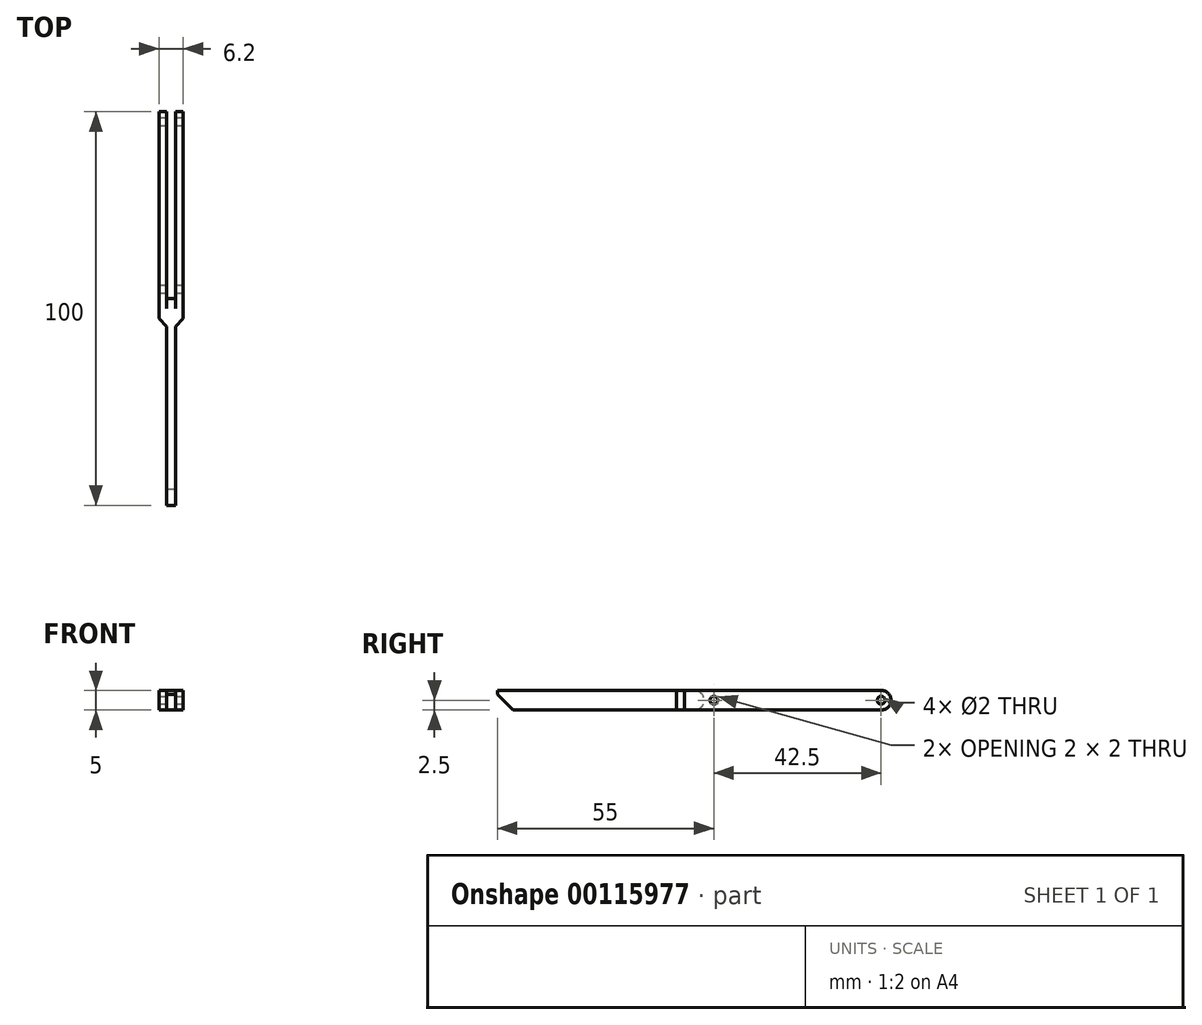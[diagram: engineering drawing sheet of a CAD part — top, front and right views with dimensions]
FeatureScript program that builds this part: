
annotation { "Feature Type Name" : "Feature", "Feature Type Description" : "" }
export const myFeature = defineFeature(function(context is Context, id is Id, definition is map)
    precondition{}
    {
        {
            var Q0;
            Q0=qCreatedBy(makeId("Top.planeOp"),FACE);
            var sketch = newSketch(context, id + "F0", { "sketchPlane" : qUnion([Q0])});
            skLineSegment(sketch, "E0", {"start": v(0, -50) * mm, "end": v(1.1, -50) * mm});
            skLineSegment(sketch, "E1", {"start": v(1.1, -50) * mm, "end": v(1.1, -2.5) * mm});
            skLineSegment(sketch, "E2", {"start": v(1.1, -2.5) * mm, "end": v(3.1, -2.5) * mm});
            skLineSegment(sketch, "E3", {"start": v(3.1, -2.5) * mm, "end": v(3.1, 50) * mm});
            skLineSegment(sketch, "E4", {"start": v(3.1, 50) * mm, "end": v(1.1, 50) * mm});
            skLineSegment(sketch, "E5", {"start": v(1.1, 50) * mm, "end": v(1.1, 2.5) * mm});
            skLineSegment(sketch, "E6", {"start": v(1.1, 2.5) * mm, "end": v(0, 2.5) * mm});
            skLineSegment(sketch, "E7.MirrorCS", {"start": v(-1.1, 2.5) * mm, "end": v(0, 2.5) * mm});
            skLineSegment(sketch, "E8.MirrorCS", {"start": v(-3.1, -2.5) * mm, "end": v(-3.1, 50) * mm});
            skLineSegment(sketch, "E9.MirrorCS", {"start": v(-1.1, -2.5) * mm, "end": v(-3.1, -2.5) * mm});
            skLineSegment(sketch, "E10.MirrorCS", {"start": v(-3.1, 50) * mm, "end": v(-1.1, 50) * mm});
            skLineSegment(sketch, "E11.MirrorCS", {"start": v(0, -50) * mm, "end": v(-1.1, -50) * mm});
            skLineSegment(sketch, "E12.MirrorCS", {"start": v(-1.1, -50) * mm, "end": v(-1.1, -2.5) * mm});
            skLineSegment(sketch, "E13.MirrorCS", {"start": v(-1.1, 50) * mm, "end": v(-1.1, 2.5) * mm});
            skSolve(sketch);
        }
        {
            var Q0;
            Q0=makeQuery(id+"F0.imprint","IMPRINT",FACE,{"disambiguationData":[TD([[makeQuery(id+"F0.imprint","IMPRINT",EDGE,{"derivedFrom":sQuery(id+"F0.wireOp",EDGE,"E0")}),1.0]])]});
            extrude(context, id + "F1", {"entities" : qUnion([Q0]), "endBound" : BoundingType.SYMMETRIC, "depth" : 5 * mm});
        }
        {
            var Q0;
            Q0=makeQuery(id+"F1.opExtrude","CAP_EDGE",EDGE,{"disambiguationData":[OSD([sQuery(id+"F0.wireOp",EDGE,"E0"),sQuery(id+"F0.wireOp",EDGE,"E11.MirrorCS")])],"isStart":true});
            chamfer(context, id + "F2", {"entities" : qUnion([Q0]), "width" : 4 * mm, "tangentPropagation" : true});
        }
        {
            var Q0;
            Q0=makeQuery(id+"F1.opExtrude","SWEPT_EDGE",EDGE,{"disambiguationData":[OSD([sQuery(id+"F0.wireOp",EDGE,"E1"),sQuery(id+"F0.wireOp",EDGE,"E2")])]});
            var Q1;
            Q1=makeQuery(id+"F1.opExtrude","SWEPT_EDGE",EDGE,{"disambiguationData":[OSD([sQuery(id+"F0.wireOp",EDGE,"E9.MirrorCS"),sQuery(id+"F0.wireOp",EDGE,"E12.MirrorCS")])]});
            chamfer(context, id + "F3", {"entities" : qUnion([Q0, Q1]), "width" : 2 * mm, "tangentPropagation" : true});
        }
        {
            var Q0;
            Q0=makeQuery(id+"F1.opExtrude","CAP_EDGE",EDGE,{"disambiguationData":[OSD([sQuery(id+"F0.wireOp",EDGE,"E4")])],"isStart":false});
            var Q1;
            Q1=makeQuery(id+"F1.opExtrude","CAP_EDGE",EDGE,{"disambiguationData":[OSD([sQuery(id+"F0.wireOp",EDGE,"E10.MirrorCS")])],"isStart":false});
            var Q2;
            Q2=makeQuery(id+"F1.opExtrude","CAP_EDGE",EDGE,{"disambiguationData":[OSD([sQuery(id+"F0.wireOp",EDGE,"E10.MirrorCS")])],"isStart":true});
            var Q3;
            Q3=makeQuery(id+"F1.opExtrude","CAP_EDGE",EDGE,{"disambiguationData":[OSD([sQuery(id+"F0.wireOp",EDGE,"E4")])],"isStart":true});
            var Q4;
            Q4=makeQuery(id+"F1.opExtrude","CAP_EDGE",EDGE,{"disambiguationData":[OSD([sQuery(id+"F0.wireOp",EDGE,"E6"),sQuery(id+"F0.wireOp",EDGE,"E7.MirrorCS")])],"isStart":true});
            var Q5;
            Q5=makeQuery(id+"F1.opExtrude","CAP_EDGE",EDGE,{"disambiguationData":[OSD([sQuery(id+"F0.wireOp",EDGE,"E6"),sQuery(id+"F0.wireOp",EDGE,"E7.MirrorCS")])],"isStart":false});
            fillet(context, id + "F4", {"entities" : qUnion([Q0, Q1, Q2, Q3, Q4, Q5]), "radius" : 2.5 * mm, "tangentPropagation" : true, "allowEdgeOverflow" : false});
        }
        {
            var Q0;
            Q0=qCreatedBy(makeId("Right.planeOp"),FACE);
            var sketch = newSketch(context, id + "F5", { "sketchPlane" : qUnion([Q0])});
            skCircle(sketch, "E14", {"center": v(5, 0) * mm, "radius": 1 * mm});
            skCircle(sketch, "E15", {"center": v(47.5, 0) * mm, "radius": 1 * mm});
            skCircle(sketch, "E16", {"center": v(5, 0) * mm, "radius": 2.5 * mm, "construction": true});
            skSolve(sketch);
        }
        {
            var Q0;
            Q0 = qSketchRegion(id + "F5", true);
            extrude(context, id + "F6", {"entities" : qUnion([Q0]), "operationType" : NewBodyOperationType.REMOVE, "endBound" : BoundingType.THROUGH_ALL, "oppositeDirection" : true, "depth" : 25 * mm, "hasSecondDirection" : true, "secondDirectionBound" : SecondDirectionBoundingType.THROUGH_ALL, "secondDirectionOppositeDirection" : false, "secondDirectionDepth" : 25 * mm});
        }
    });
